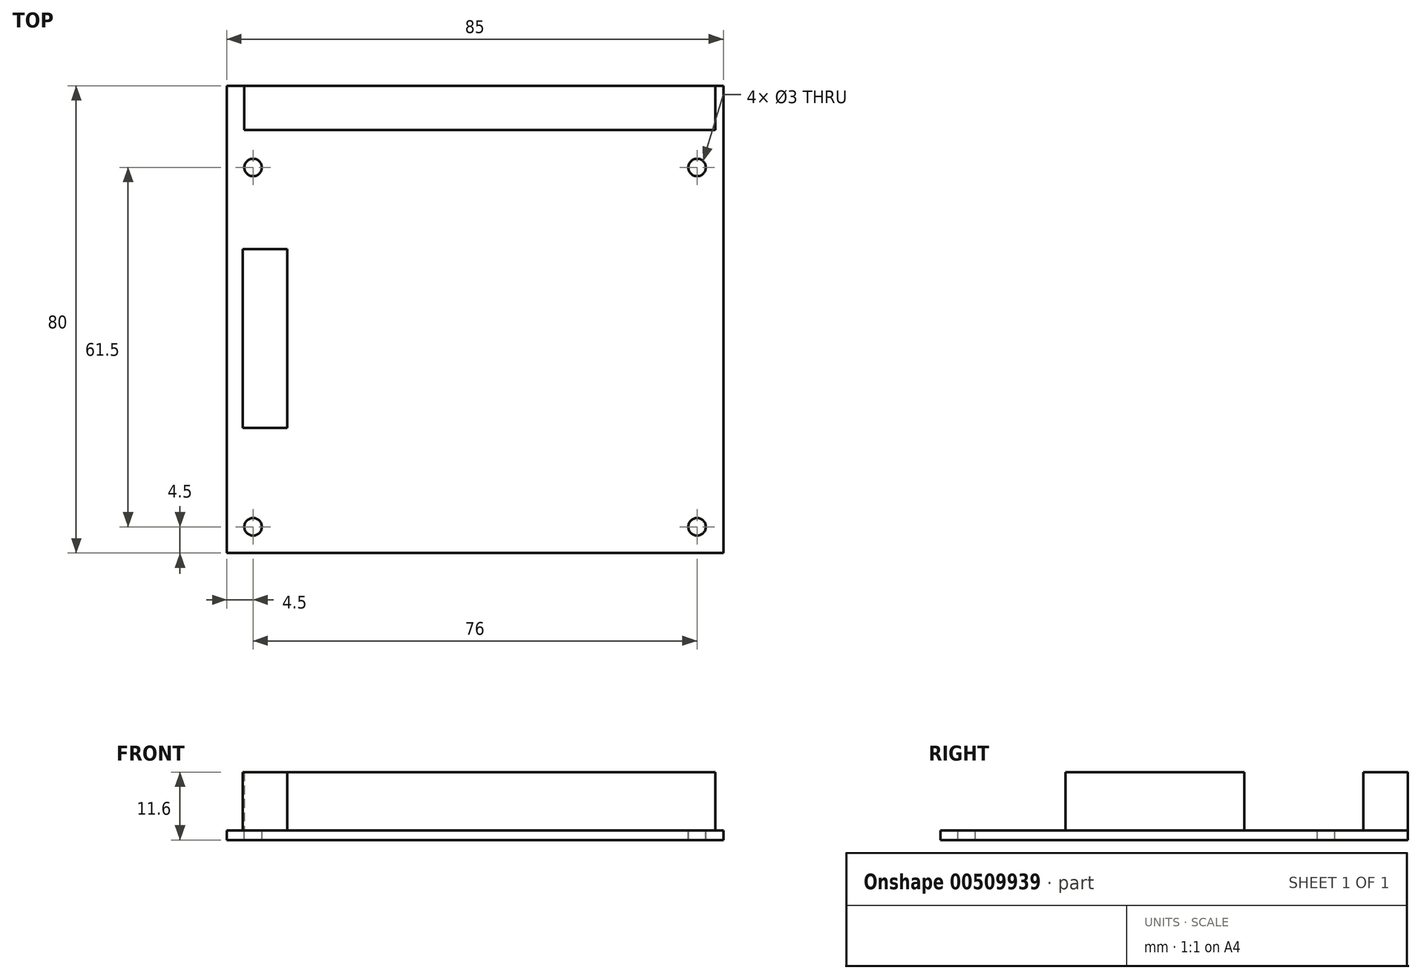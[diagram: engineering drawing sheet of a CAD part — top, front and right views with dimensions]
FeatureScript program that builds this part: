
annotation { "Feature Type Name" : "Feature", "Feature Type Description" : "" }
export const myFeature = defineFeature(function(context is Context, id is Id, definition is map)
    precondition{}
    {
        {
            var Q0;
            Q0=qCreatedBy(makeId("Top.planeOp"),FACE);
            var sketch = newSketch(context, id + "F0", { "sketchPlane" : qUnion([Q0])});
            skLineSegment(sketch, "E0.bottom", {"start": v(-42.5, 40) * mm, "end": v(42.5, 40) * mm});
            skLineSegment(sketch, "E0.top", {"start": v(-42.5, -40) * mm, "end": v(42.5, -40) * mm});
            skLineSegment(sketch, "E0.left", {"start": v(-42.5, 40) * mm, "end": v(-42.5, -40) * mm});
            skLineSegment(sketch, "E0.right", {"start": v(42.5, 40) * mm, "end": v(42.5, -40) * mm});
            skPoint(sketch, "E0.middle", {"position": v(0, 0) * mm});
            skSolve(sketch);
        }
        {
            var Q0;
            Q0=qSketchRegion(id+"F0",true);
            extrude(context, id + "F1", {"entities" : qUnion([Q0]), "depth" : 1.6 * mm});
        }
        {
            var Q0;
            Q0=makeQuery(id+"F1.opExtrude","CAP_FACE",FACE,{"disambiguationData":[OSD([sQuery(id+"F0.wireOp",EDGE,"E0.bottom"),sQuery(id+"F0.wireOp",EDGE,"E0.top"),sQuery(id+"F0.wireOp",EDGE,"E0.left"),sQuery(id+"F0.wireOp",EDGE,"E0.right")])],"isStart":false});
            var sketch = newSketch(context, id + "F2", { "sketchPlane" : qUnion([Q0])});
            skLineSegment(sketch, "E1.bottom", {"start": v(-39.75, 12) * mm, "end": v(-32.15, 12) * mm});
            skLineSegment(sketch, "E1.top", {"start": v(-39.75, -18.6) * mm, "end": v(-32.15, -18.6) * mm});
            skLineSegment(sketch, "E1.left", {"start": v(-39.75, 12) * mm, "end": v(-39.75, -18.6) * mm});
            skLineSegment(sketch, "E1.right", {"start": v(-32.15, 12) * mm, "end": v(-32.15, -18.6) * mm});
            skSolve(sketch);
        }
        {
            var Q0;
            Q0=qSketchRegion(id+"F2",true);
            extrude(context, id + "F3", {"entities" : qUnion([Q0]), "operationType" : NewBodyOperationType.ADD, "depth" : 10 * mm});
        }
        {
            var Q0;
            Q0=makeQuery(id+"F1.opExtrude","CAP_FACE",FACE,{"disambiguationData":[OSD([sQuery(id+"F0.wireOp",EDGE,"E0.bottom"),sQuery(id+"F0.wireOp",EDGE,"E0.top"),sQuery(id+"F0.wireOp",EDGE,"E0.left"),sQuery(id+"F0.wireOp",EDGE,"E0.right")])],"isStart":false});
            var sketch = newSketch(context, id + "F4", { "sketchPlane" : qUnion([Q0])});
            skCircle(sketch, "E2", {"center": v(-38, 26) * mm, "radius": 1.5 * mm});
            skSolve(sketch);
        }
        {
            var Q0;
            Q0=sQuery(id+"F4.wireOp",VERTEX,"E2.center");
            var Q1;
            Q1=makeQuery(id+"F1.opExtrude","SWEPT_BODY",BODY,{"disambiguationData":[OSD([sQuery(id+"F0.wireOp",EDGE,"E0.bottom"),sQuery(id+"F0.wireOp",EDGE,"E0.top"),sQuery(id+"F0.wireOp",EDGE,"E0.left"),sQuery(id+"F0.wireOp",EDGE,"E0.right")])]});
            hole(context, id + "F5", {"style" : HoleStyle.SIMPLE, "endStyle" : HoleEndStyle.THROUGH, "holeDiameter" : 3 * mm, "isTappedThrough" : true, "tappedDepth" : 12 * mm, "tapClearance" : 3, "locations" : qUnion([Q0]), "scope" : qUnion([Q1])});
        }
        {
            var Q0;
            Q0=qCreatedBy(makeId("Top.planeOp"),FACE);
            var sketch = newSketch(context, id + "F6", { "sketchPlane" : qUnion([Q0])});
            skCircle(sketch, "E3", {"center": v(38, 26) * mm, "radius": 1.5 * mm});
            skSolve(sketch);
        }
        {
            var Q0;
            Q0=sQuery(id+"F6.wireOp",VERTEX,"E3.center");
            var Q1;
            Q1=makeQuery(id+"F1.opExtrude","SWEPT_BODY",BODY,{"disambiguationData":[OSD([sQuery(id+"F0.wireOp",EDGE,"E0.bottom"),sQuery(id+"F0.wireOp",EDGE,"E0.top"),sQuery(id+"F0.wireOp",EDGE,"E0.left"),sQuery(id+"F0.wireOp",EDGE,"E0.right")])]});
            hole(context, id + "F7", {"style" : HoleStyle.SIMPLE, "endStyle" : HoleEndStyle.THROUGH, "oppositeDirection" : true, "holeDiameter" : 3 * mm, "isTappedThrough" : true, "tappedDepth" : 12 * mm, "tapClearance" : 3, "locations" : qUnion([Q0]), "scope" : qUnion([Q1])});
        }
        {
            var Q0;
            Q0=makeQuery(id+"F1.opExtrude","CAP_FACE",FACE,{"disambiguationData":[OSD([sQuery(id+"F0.wireOp",EDGE,"E0.bottom"),sQuery(id+"F0.wireOp",EDGE,"E0.top"),sQuery(id+"F0.wireOp",EDGE,"E0.left"),sQuery(id+"F0.wireOp",EDGE,"E0.right")])],"isStart":false});
            var sketch = newSketch(context, id + "F8", { "sketchPlane" : qUnion([Q0])});
            skCircle(sketch, "E4", {"center": v(38, -35.5) * mm, "radius": 1.5 * mm});
            skSolve(sketch);
        }
        {
            var Q0;
            Q0=sQuery(id+"F8.wireOp",VERTEX,"E4.center");
            var Q1;
            Q1=makeQuery(id+"F1.opExtrude","SWEPT_BODY",BODY,{"disambiguationData":[OSD([sQuery(id+"F0.wireOp",EDGE,"E0.bottom"),sQuery(id+"F0.wireOp",EDGE,"E0.top"),sQuery(id+"F0.wireOp",EDGE,"E0.left"),sQuery(id+"F0.wireOp",EDGE,"E0.right")])]});
            hole(context, id + "F9", {"style" : HoleStyle.SIMPLE, "endStyle" : HoleEndStyle.THROUGH, "holeDiameter" : 3 * mm, "isTappedThrough" : true, "tappedDepth" : 12 * mm, "tapClearance" : 3, "locations" : qUnion([Q0]), "scope" : qUnion([Q1])});
        }
        {
            var Q0;
            Q0=makeQuery(id+"F1.opExtrude","CAP_FACE",FACE,{"disambiguationData":[OSD([sQuery(id+"F0.wireOp",EDGE,"E0.bottom"),sQuery(id+"F0.wireOp",EDGE,"E0.top"),sQuery(id+"F0.wireOp",EDGE,"E0.left"),sQuery(id+"F0.wireOp",EDGE,"E0.right")])],"isStart":false});
            var sketch = newSketch(context, id + "F10", { "sketchPlane" : qUnion([Q0])});
            skCircle(sketch, "E5", {"center": v(-38, -35.5) * mm, "radius": 1.5 * mm});
            skSolve(sketch);
        }
        {
            var Q0;
            Q0=sQuery(id+"F10.wireOp",VERTEX,"E5.center");
            var Q1;
            Q1=makeQuery(id+"F1.opExtrude","SWEPT_BODY",BODY,{"disambiguationData":[OSD([sQuery(id+"F0.wireOp",EDGE,"E0.bottom"),sQuery(id+"F0.wireOp",EDGE,"E0.top"),sQuery(id+"F0.wireOp",EDGE,"E0.left"),sQuery(id+"F0.wireOp",EDGE,"E0.right")])]});
            hole(context, id + "F11", {"style" : HoleStyle.SIMPLE, "endStyle" : HoleEndStyle.THROUGH, "holeDiameter" : 3 * mm, "isTappedThrough" : true, "tappedDepth" : 12 * mm, "tapClearance" : 3, "locations" : qUnion([Q0]), "scope" : qUnion([Q1])});
        }
        {
            var Q0;
            Q0=makeQuery(id+"F1.opExtrude","SWEPT_BODY",BODY,{"disambiguationData":[OSD([sQuery(id+"F0.wireOp",EDGE,"E0.bottom"),sQuery(id+"F0.wireOp",EDGE,"E0.top"),sQuery(id+"F0.wireOp",EDGE,"E0.left"),sQuery(id+"F0.wireOp",EDGE,"E0.right")])]});
            transform(context, id + "F12", {"entities" : qUnion([Q0]), "transformType" : TransformType.TRANSLATION_3D, "dx" : 0 * mm, "dy" : 0 * mm, "dz" : 0 * mm, "makeCopy" : true});
        }
        {
            var Q0;
            Q0=makeQuery(id+"F12.opPattern","COPY",BODY,{"derivedFrom":makeQuery(id+"F1.opExtrude","SWEPT_BODY",BODY,{"disambiguationData":[OSD([sQuery(id+"F0.wireOp",EDGE,"E0.bottom"),sQuery(id+"F0.wireOp",EDGE,"E0.top"),sQuery(id+"F0.wireOp",EDGE,"E0.left"),sQuery(id+"F0.wireOp",EDGE,"E0.right")])]}),"instanceName":"1"});
            deleteBodies(context, id + "F13", {"entities" : qUnion([Q0])});
        }
        {
            var Q0;
            Q0=makeQuery(id+"F1.opExtrude","CAP_FACE",FACE,{"disambiguationData":[OSD([sQuery(id+"F0.wireOp",EDGE,"E0.bottom"),sQuery(id+"F0.wireOp",EDGE,"E0.top"),sQuery(id+"F0.wireOp",EDGE,"E0.left"),sQuery(id+"F0.wireOp",EDGE,"E0.right")])],"isStart":false});
            var sketch = newSketch(context, id + "F14", { "sketchPlane" : qUnion([Q0])});
            skLineSegment(sketch, "E6.bottom", {"start": v(-39.5, 40) * mm, "end": v(41.1, 40) * mm});
            skLineSegment(sketch, "E6.top", {"start": v(-39.5, 32.4) * mm, "end": v(41.1, 32.4) * mm});
            skLineSegment(sketch, "E6.left", {"start": v(-39.5, 40) * mm, "end": v(-39.5, 32.4) * mm});
            skLineSegment(sketch, "E6.right", {"start": v(41.1, 40) * mm, "end": v(41.1, 32.4) * mm});
            skSolve(sketch);
        }
        {
            var Q0;
            Q0 = qSketchRegion(id + "F14", true);
            extrude(context, id + "F15", {"entities" : qUnion([Q0]), "operationType" : NewBodyOperationType.ADD, "depth" : 10 * mm});
        }
    });
